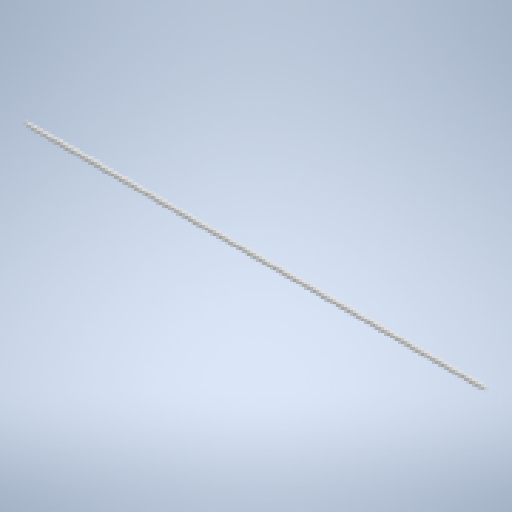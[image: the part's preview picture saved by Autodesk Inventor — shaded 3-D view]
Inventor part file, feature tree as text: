
AUTODESK INVENTOR PART (.ipt)
format: ipt  version: 2023 (Build 270158000, 158)  size: 162,304 bytes
history: native  units: in
note: dims shown in document units (in); Inventor stores cm internally (conversion verified against a paired STEP export)
features: revolve x1, sketch x1
ambient origin geometry x8: Origin, YZ Plane, XZ Plane, XY Plane, X Axis, Y Axis, Z Axis, Center Point
bodies: Solid1 (feature_tree)
feature tree (2):
  revolve  "Revolution1"  [1 undecoded]
  sketch  "Sketch1"  dims[d0=0.1575in d1=0.1969in d2=0.2362in d3=135.0deg d4=135.0deg d5=0.5906in d6=1.5354in d7=135.0deg d8=0.1575in d9=0.2756in d10=0.3937in d11=0.0079in d12=0.0354in d14=135.0deg d15=47.2441in d16=90.0deg]
note: 1 required parameter value undecoded (feature->parameter linkage not recoverable at this tier; creation-order binding heuristic only, values carry confidence <= 0.55)
